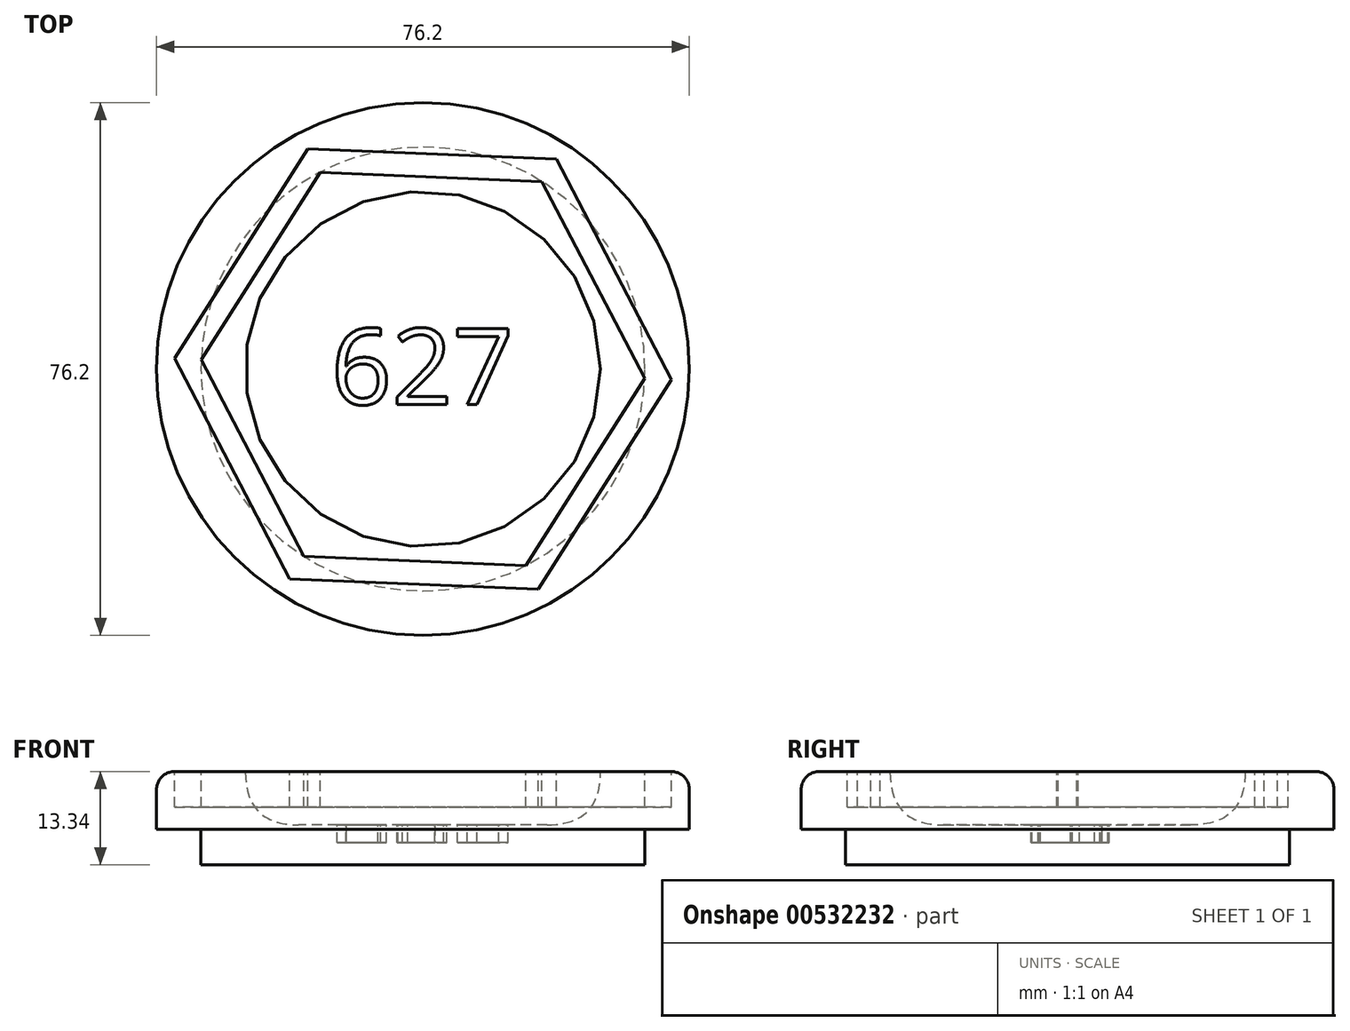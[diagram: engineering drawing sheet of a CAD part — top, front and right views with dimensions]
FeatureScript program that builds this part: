
annotation { "Feature Type Name" : "Feature", "Feature Type Description" : "" }
export const myFeature = defineFeature(function(context is Context, id is Id, definition is map)
    precondition{}
    {
        {
            var Q0;
            Q0=qCreatedBy(makeId("Top.planeOp"),FACE);
            var sketch = newSketch(context, id + "F0", { "sketchPlane" : qUnion([Q0])});
            skCircle(sketch, "E0", {"center": v(0, 0) * mm, "radius": 38.1 * mm});
            skSolve(sketch);
        }
        {
            var Q0;
            Q0 = qSketchRegion(id + "F0", true);
            extrude(context, id + "F1", {"entities" : qUnion([Q0]), "depth" : 15.88 * mm, "offsetDistance" : 25.4 * mm});
        }
        {
            var Q0;
            Q0=makeQuery(id+"F1.opExtrude","CAP_FACE",FACE,{"disambiguationData":[OSD([sQuery(id+"F0.wireOp",EDGE,"E0")])],"isStart":false});
            var sketch = newSketch(context, id + "F2", { "sketchPlane" : qUnion([Q0])});
            skCircle(sketch, "E1.cCircle", {"center": v(0, 0) * mm, "radius": 31.75 * mm, "construction": true});
            skLineSegment(sketch, "E1.0", {"start": v(14.7, -28.14) * mm, "end": v(-17.02, -26.8) * mm});
            skLineSegment(sketch, "E1.1", {"start": v(-17.02, -26.8) * mm, "end": v(-31.72, 1.34) * mm});
            skLineSegment(sketch, "E1.2", {"start": v(-31.72, 1.34) * mm, "end": v(-14.7, 28.14) * mm});
            skLineSegment(sketch, "E1.3", {"start": v(-14.7, 28.14) * mm, "end": v(17.02, 26.8) * mm});
            skLineSegment(sketch, "E1.4", {"start": v(17.02, 26.8) * mm, "end": v(31.72, -1.34) * mm});
            skLineSegment(sketch, "E1.5", {"start": v(31.72, -1.34) * mm, "end": v(14.7, -28.14) * mm});
            skLineSegment(sketch, "E2.0", {"start": v(-19.07, -30.02) * mm, "end": v(-35.53, 1.5) * mm});
            skLineSegment(sketch, "E2.1", {"start": v(-16.46, 31.52) * mm, "end": v(19.07, 30.02) * mm});
            skLineSegment(sketch, "E2.2", {"start": v(19.07, 30.02) * mm, "end": v(35.53, -1.5) * mm});
            skLineSegment(sketch, "E2.3", {"start": v(-35.53, 1.5) * mm, "end": v(-16.46, 31.52) * mm});
            skLineSegment(sketch, "E2.4", {"start": v(35.53, -1.5) * mm, "end": v(16.46, -31.52) * mm});
            skLineSegment(sketch, "E2.5", {"start": v(16.46, -31.52) * mm, "end": v(-19.07, -30.02) * mm});
            skCircle(sketch, "E3", {"center": v(0, 0) * mm, "radius": 25.4 * mm});
            skSolve(sketch);
        }
        {
            var Q0;
            Q0 = qSketchRegion(id + "F2", true);
            extrude(context, id + "F3", {"entities" : qUnion([Q0]), "operationType" : NewBodyOperationType.REMOVE, "oppositeDirection" : true, "depth" : 5.08 * mm, "offsetDistance" : 25.4 * mm});
        }
        {
            var Q0;
            Q0=makeQuery(id+"F2.imprint","IMPRINT",FACE,{"disambiguationData":[TD([[makeQuery(id+"F2.imprint","IMPRINT",EDGE,{"derivedFrom":sQuery(id+"F2.wireOp",EDGE,"E3")}),1.0]])]});
            extrude(context, id + "F4", {"entities" : qUnion([Q0]), "operationType" : NewBodyOperationType.REMOVE, "oppositeDirection" : true, "depth" : 7.62 * mm, "offsetDistance" : 25.4 * mm});
        }
        {
            var Q0;
            Q0=makeQuery(id+"F4.boolean.opBoolean","COPY",EDGE,{"derivedFrom":makeQuery(id+"F4.opExtrude","CAP_EDGE",EDGE,{"disambiguationData":[OSD([sQuery(id+"F2.wireOp",EDGE,"E3")])],"isStart":false})});
            fillet(context, id + "F5", {"entities" : qUnion([Q0]), "radius" : 7.62 * mm, "tangentPropagation" : true, "rho" : 0.5, "crossSection" : FilletCrossSection.CONIC, "allowEdgeOverflow" : false});
        }
        {
            var Q0;
            Q0=makeQuery(id+"F4.boolean.opBoolean","COPY",FACE,{"derivedFrom":makeQuery(id+"F4.opExtrude","CAP_FACE",FACE,{"disambiguationData":[OSD([sQuery(id+"F2.wireOp",EDGE,"E3")])],"isStart":false})});
            var sketch = newSketch(context, id + "F6", { "sketchPlane" : qUnion([Q0])});
            skText(sketch, "E4", { "text": "627", "fontName": "OpenSans-Regular.ttf"});
            const initialGuessF6  = {"E4": [-0.01315, -0.00508, 1, 0, 0.01095]};
            skSetInitialGuess(sketch, initialGuessF6);
            skSolve(sketch);
        }
        {
            var Q0;
            Q0 = qSketchRegion(id + "F6", true);
            extrude(context, id + "F7", {"entities" : qUnion([Q0]), "operationType" : NewBodyOperationType.REMOVE, "oppositeDirection" : true, "depth" : 2.54 * mm, "offsetDistance" : 25.4 * mm});
        }
        {
            var Q0;
            Q0=qCreatedBy(makeId("Top.planeOp"),FACE);
            var sketch = newSketch(context, id + "F8", { "sketchPlane" : qUnion([Q0])});
            skCircle(sketch, "E5", {"center": v(0, 0) * mm, "radius": 31.75 * mm});
            skSolve(sketch);
        }
        {
            var Q0;
            Q0=makeQuery(id+"F8.imprint","IMPRINT",FACE,{"disambiguationData":[TD([[makeQuery(id+"F8.imprint","IMPRINT",EDGE,{"derivedFrom":sQuery(id+"F8.wireOp",EDGE,"E5")}),1.0]])]});
            extrude(context, id + "F9", {"entities" : qUnion([Q0]), "operationType" : NewBodyOperationType.REMOVE, "depth" : 2.54 * mm, "offsetDistance" : 25.4 * mm});
        }
        {
            var Q0;
            Q0=makeQuery(id+"F1.opExtrude","CAP_FACE",FACE,{"disambiguationData":[OSD([sQuery(id+"F0.wireOp",EDGE,"E0")])],"isStart":true});
            extrude(context, id + "F10", {"entities" : qUnion([Q0]), "operationType" : NewBodyOperationType.REMOVE, "oppositeDirection" : true, "depth" : 7.62 * mm, "offsetDistance" : 25.4 * mm});
        }
        {
            var Q0;
            Q0=makeQuery(id+"F1.opExtrude","CAP_EDGE",EDGE,{"disambiguationData":[OSD([sQuery(id+"F0.wireOp",EDGE,"E0")])],"isStart":false});
            fillet(context, id + "F11", {"entities" : qUnion([Q0]), "tangentPropagation" : true, "radius" : 2.54 * mm, "defaultsChanged" : true, "vertexSettings" : [], "allowEdgeOverflow" : false});
        }
    });
